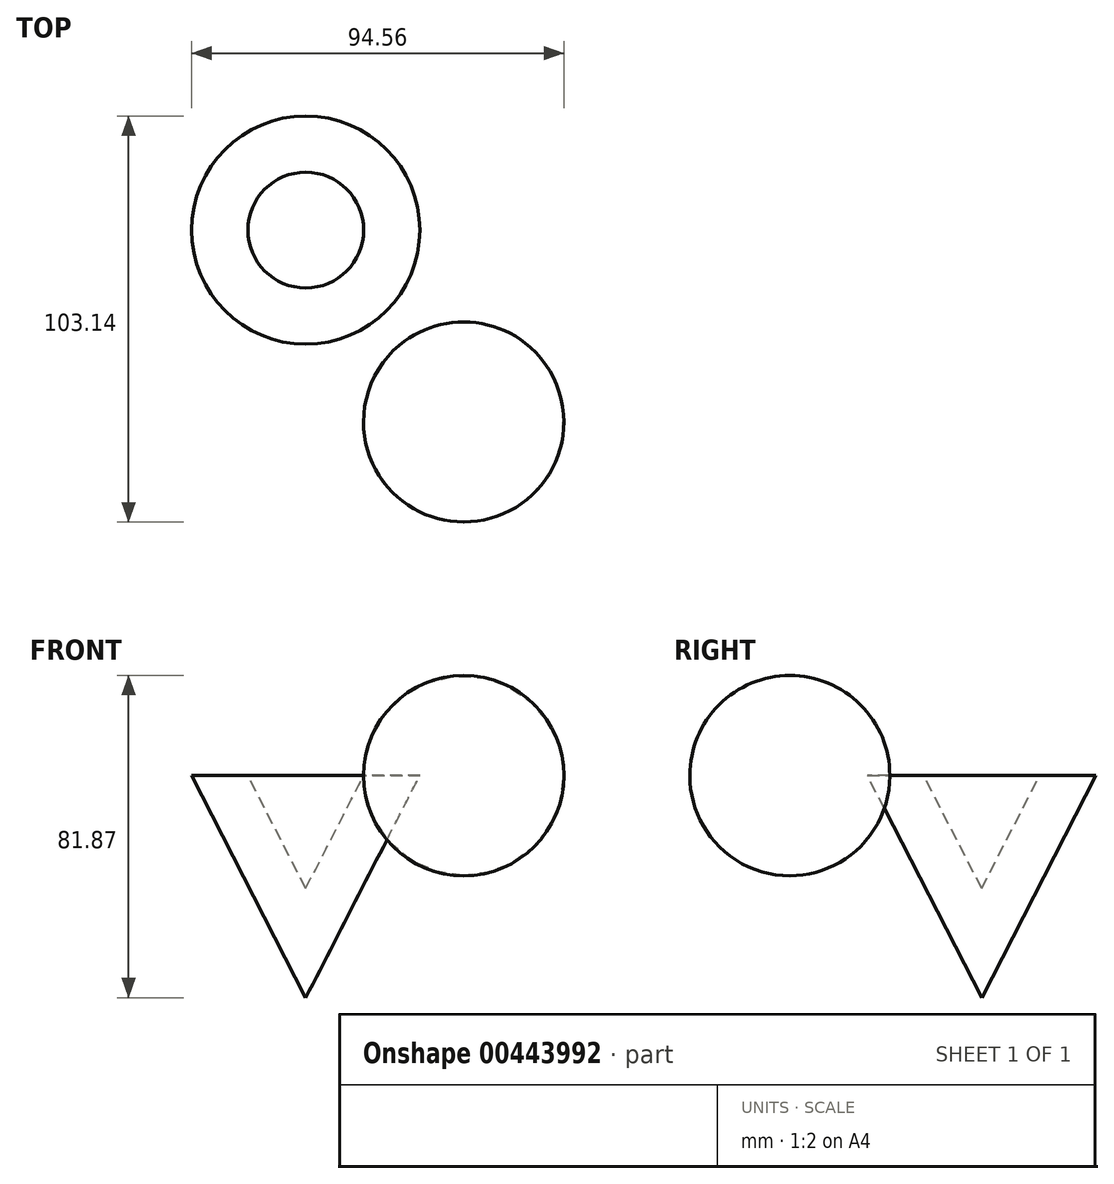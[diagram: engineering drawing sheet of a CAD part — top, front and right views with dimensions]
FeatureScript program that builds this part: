
annotation { "Feature Type Name" : "Feature", "Feature Type Description" : "" }
export const myFeature = defineFeature(function(context is Context, id is Id, definition is map)
    precondition{}
    {
        {
            var Q0;
            Q0=qCreatedBy(makeId("Right.planeOp"),FACE);
            var sketch = newSketch(context, id + "F0", { "sketchPlane" : qUnion([Q0])});
            skLineSegment(sketch, "E0", {"start": v(0, 0) * mm, "end": v(-29, 0) * mm});
            skLineSegment(sketch, "E1", {"start": v(-29, 0) * mm, "end": v(0, -56.42) * mm});
            skLineSegment(sketch, "E2", {"start": v(0, -56.42) * mm, "end": v(0, 0) * mm});
            skSolve(sketch);
        }
        {
            var Q0;
            Q0 = qSketchRegion(id + "F0", true);
            var Q1;
            Q1=sQuery(id+"F0.wireOp",EDGE,"E2");
            revolve(context, id + "F1", {"entities" : qUnion([Q0]), "axis" : qUnion([Q1]), "revolveType" : RevolveType.FULL});
        }
        {
            var Q0;
            Q0=makeQuery(id+"F1.opRevolve","SWEPT_FACE",FACE,{"disambiguationData":[OSD([sQuery(id+"F0.wireOp",EDGE,"E0")])]});
            shell(context, id + "F2", {"entities" : qUnion([Q0]), "thickness" : 12.7 * mm});
        }
        {
            var Q0;
            Q0=qCreatedBy(makeId("Top.planeOp"),FACE);
            var sketch = newSketch(context, id + "F3", { "sketchPlane" : qUnion([Q0])});
            skCircle(sketch, "E3", {"center": v(40.08, -48.74) * mm, "radius": 25.4 * mm});
            skLineSegment(sketch, "E4", {"start": v(40.12, -23.34) * mm, "end": v(40.12, -74.15) * mm});
            skSolve(sketch);
        }
        {
            var Q0;
            {var subQ0=sQuery(id+"F3.wireOp",EDGE,"E4");Q0=makeQuery(id+"F3.imprint","IMPRINT",FACE,{"disambiguationData":[TD([[makeQuery(id+"F3.imprint","IMPRINT",EDGE,{"derivedFrom":subQ0}),1.0]])]});}
            var Q1;
            Q1=sQuery(id+"F3.wireOp",EDGE,"E4");
            revolve(context, id + "F4", {"entities" : qUnion([Q0]), "axis" : qUnion([Q1]), "revolveType" : RevolveType.FULL});
        }
    });
